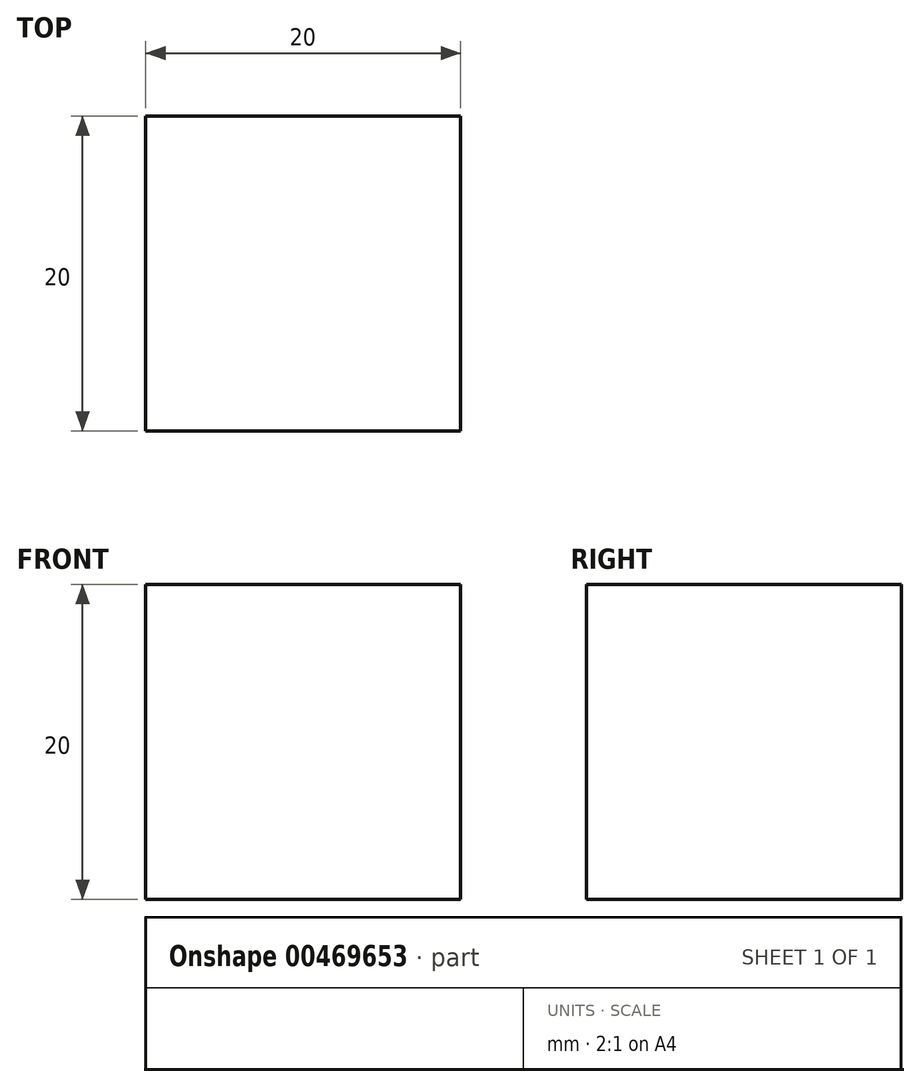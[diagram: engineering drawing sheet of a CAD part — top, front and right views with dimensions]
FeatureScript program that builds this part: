
annotation { "Feature Type Name" : "Feature", "Feature Type Description" : "" }
export const myFeature = defineFeature(function(context is Context, id is Id, definition is map)
    precondition{}
    {
        {
            var Q0;
            Q0=qCreatedBy(makeId("Front.planeOp"),FACE);
            var sketch = newSketch(context, id + "F0", { "sketchPlane" : qUnion([Q0])});
            skLineSegment(sketch, "E0.bottom", {"start": v(0, 0) * mm, "end": v(-20, 0) * mm});
            skLineSegment(sketch, "E0.top", {"start": v(0, 20) * mm, "end": v(-20, 20) * mm});
            skLineSegment(sketch, "E0.left", {"start": v(0, 0) * mm, "end": v(0, 20) * mm});
            skLineSegment(sketch, "E0.right", {"start": v(-20, 0) * mm, "end": v(-20, 20) * mm});
            skSolve(sketch);
        }
        {
            var Q0;
            Q0 = qSketchRegion(id + "F0", true);
            extrude(context, id + "F1", {"entities" : qUnion([Q0]), "depth" : 20 * mm});
        }
    });
